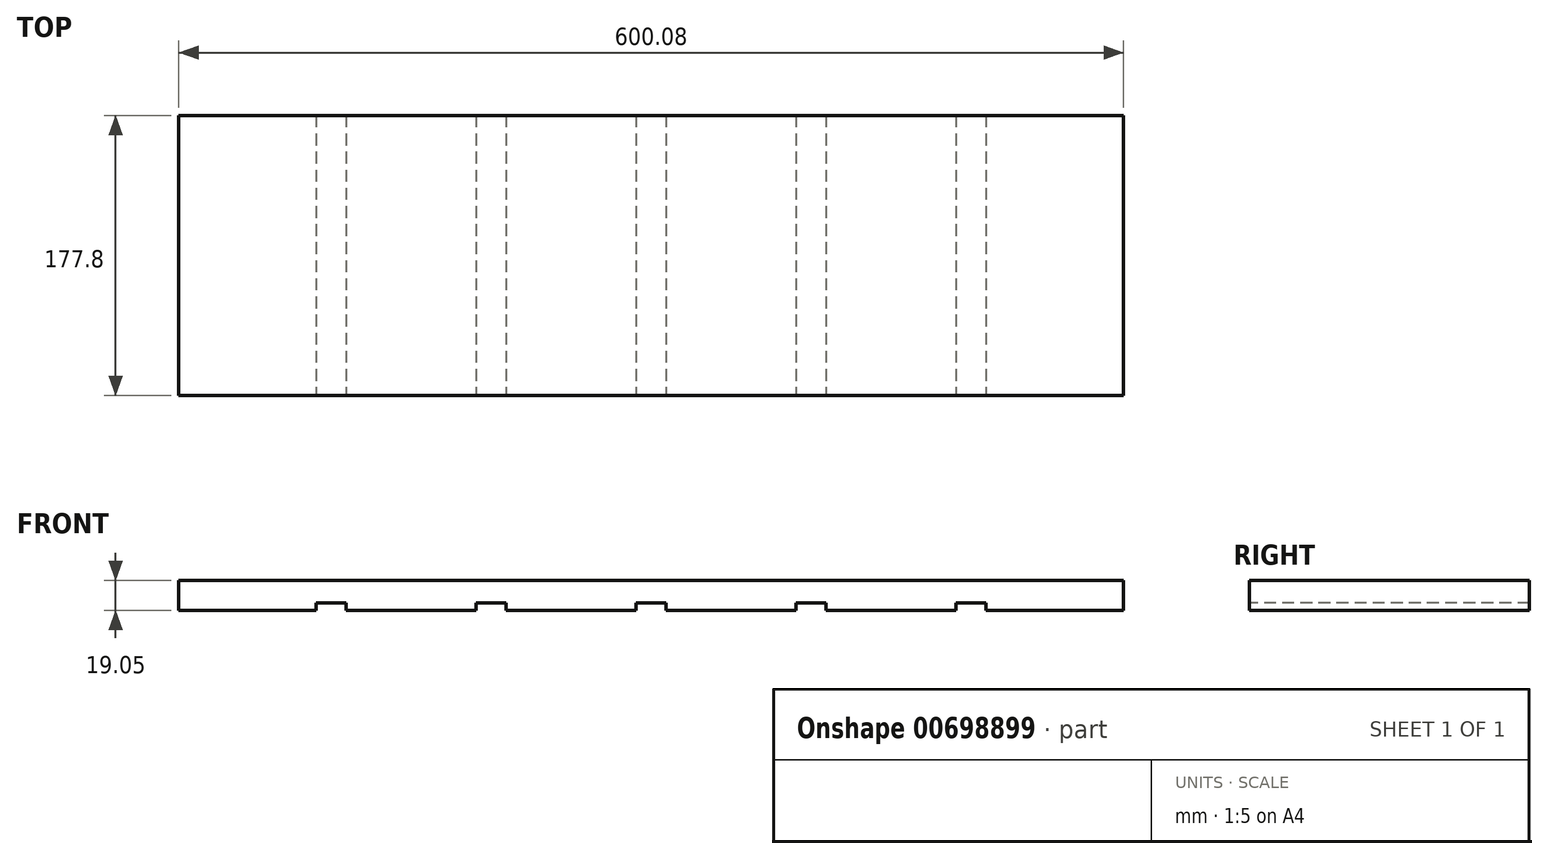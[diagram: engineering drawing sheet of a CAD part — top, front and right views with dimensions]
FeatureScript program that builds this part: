
annotation { "Feature Type Name" : "Feature", "Feature Type Description" : "" }
export const myFeature = defineFeature(function(context is Context, id is Id, definition is map)
    precondition{}
    {
        {
            var Q0;
            Q0=qCreatedBy(makeId("Front.planeOp"),FACE);
            var sketch = newSketch(context, id + "F0", { "sketchPlane" : qUnion([Q0])});
            skLineSegment(sketch, "E0.bottom", {"start": v(0, 0) * mm, "end": v(600.08, 0) * mm});
            skLineSegment(sketch, "E0.top", {"start": v(0, 19.05) * mm, "end": v(600.08, 19.05) * mm});
            skLineSegment(sketch, "E0.left", {"start": v(0, 0) * mm, "end": v(0, 19.05) * mm});
            skLineSegment(sketch, "E0.right", {"start": v(600.08, 0) * mm, "end": v(600.08, 19.05) * mm});
            skSolve(sketch);
        }
        {
            var Q0;
            Q0=qCreatedBy(makeId("Front.planeOp"),FACE);
            var sketch = newSketch(context, id + "F1", { "sketchPlane" : qUnion([Q0])});
            skLineSegment(sketch, "E1.bottom", {"start": v(87.31, 0) * mm, "end": v(106.36, 0) * mm});
            skLineSegment(sketch, "E1.top", {"start": v(87.31, 4.76) * mm, "end": v(106.36, 4.76) * mm});
            skLineSegment(sketch, "E1.left", {"start": v(87.31, 0) * mm, "end": v(87.31, 4.76) * mm});
            skLineSegment(sketch, "E1.right", {"start": v(106.36, 0) * mm, "end": v(106.36, 4.76) * mm});
            skLineSegment(sketch, "E2.1.0.0", {"start": v(188.91, 4.76) * mm, "end": v(207.96, 4.76) * mm});
            skLineSegment(sketch, "E2.1.0.1", {"start": v(188.91, 0) * mm, "end": v(188.91, 4.76) * mm});
            skLineSegment(sketch, "E2.1.0.2", {"start": v(188.91, 0) * mm, "end": v(207.96, 0) * mm});
            skLineSegment(sketch, "E2.1.0.3", {"start": v(207.96, 0) * mm, "end": v(207.96, 4.76) * mm});
            skLineSegment(sketch, "E2.2.0.0", {"start": v(290.51, 4.76) * mm, "end": v(309.56, 4.76) * mm});
            skLineSegment(sketch, "E2.2.0.1", {"start": v(290.51, 0) * mm, "end": v(290.51, 4.76) * mm});
            skLineSegment(sketch, "E2.2.0.2", {"start": v(290.51, 0) * mm, "end": v(309.56, 0) * mm});
            skLineSegment(sketch, "E2.2.0.3", {"start": v(309.56, 0) * mm, "end": v(309.56, 4.76) * mm});
            skLineSegment(sketch, "E2.3.0.0", {"start": v(392.11, 4.76) * mm, "end": v(411.16, 4.76) * mm});
            skLineSegment(sketch, "E2.3.0.1", {"start": v(392.11, 0) * mm, "end": v(392.11, 4.76) * mm});
            skLineSegment(sketch, "E2.3.0.2", {"start": v(392.11, 0) * mm, "end": v(411.16, 0) * mm});
            skLineSegment(sketch, "E2.3.0.3", {"start": v(411.16, 0) * mm, "end": v(411.16, 4.76) * mm});
            skLineSegment(sketch, "E2.4.0.0", {"start": v(493.71, 4.76) * mm, "end": v(512.76, 4.76) * mm});
            skLineSegment(sketch, "E2.4.0.1", {"start": v(493.71, 0) * mm, "end": v(493.71, 4.76) * mm});
            skLineSegment(sketch, "E2.4.0.2", {"start": v(493.71, 0) * mm, "end": v(512.76, 0) * mm});
            skLineSegment(sketch, "E2.4.0.3", {"start": v(512.76, 0) * mm, "end": v(512.76, 4.76) * mm});
            skLineSegment(sketch, "E2.direction1", {"start": v(87.31, 0) * mm, "end": v(188.91, 0) * mm, "construction": true});
            skSolve(sketch);
        }
        {
            var Q0;
            Q0=qSketchRegion(id+"F0",true);
            extrude(context, id + "F2", {"entities" : qUnion([Q0]), "oppositeDirection" : true, "depth" : 177.8 * mm, "offsetDistance" : 25.4 * mm});
        }
        {
            var Q0;
            Q0 = qSketchRegion(id + "F1", true);
            extrude(context, id + "F3", {"entities" : qUnion([Q0]), "operationType" : NewBodyOperationType.REMOVE, "endBound" : BoundingType.THROUGH_ALL, "oppositeDirection" : true, "depth" : 25.4 * mm, "offsetDistance" : 25.4 * mm});
        }
    });
